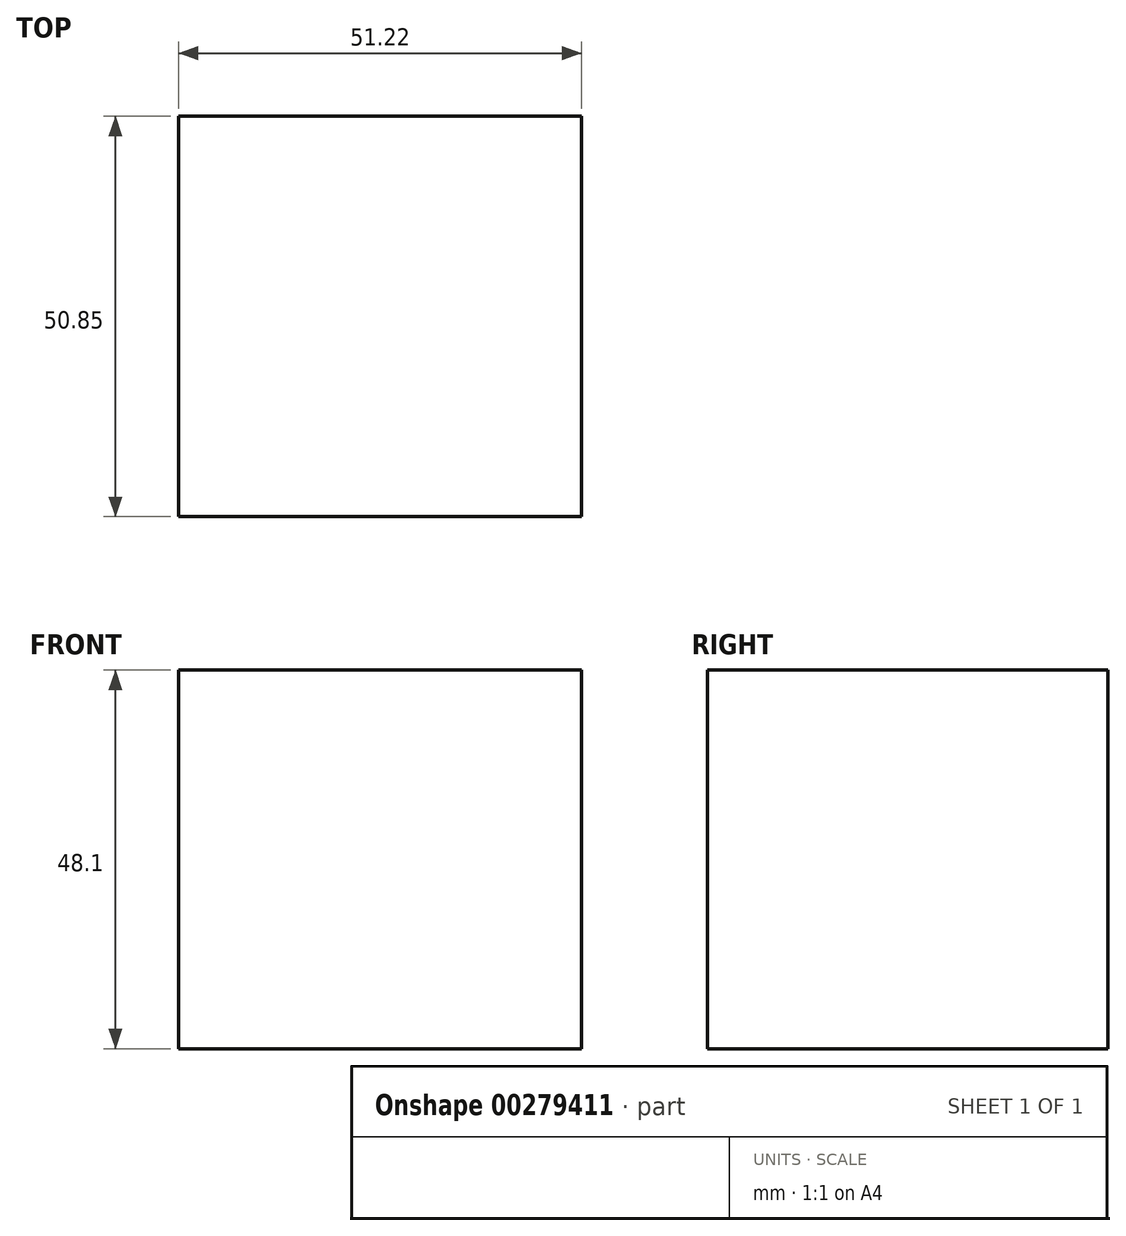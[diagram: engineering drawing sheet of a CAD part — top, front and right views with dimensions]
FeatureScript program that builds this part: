
annotation { "Feature Type Name" : "Feature", "Feature Type Description" : "" }
export const myFeature = defineFeature(function(context is Context, id is Id, definition is map)
    precondition{}
    {
        {
            var Q0;
            Q0=qCreatedBy(makeId("Top.planeOp"),FACE);
            var sketch = newSketch(context, id + "F0", { "sketchPlane" : qUnion([Q0])});
            skLineSegment(sketch, "E0.bottom", {"start": v(0, 0) * mm, "end": v(51.22, 0) * mm});
            skLineSegment(sketch, "E0.top", {"start": v(0, 50.85) * mm, "end": v(51.22, 50.85) * mm});
            skLineSegment(sketch, "E0.left", {"start": v(0, 0) * mm, "end": v(0, 50.85) * mm});
            skLineSegment(sketch, "E0.right", {"start": v(51.22, 0) * mm, "end": v(51.22, 50.85) * mm});
            skSolve(sketch);
        }
        {
            var Q0;
            Q0=makeQuery(id+"F0.imprint","IMPRINT",FACE,{"disambiguationData":[TD([[makeQuery(id+"F0.imprint","IMPRINT",EDGE,{"derivedFrom":sQuery(id+"F0.wireOp",EDGE,"E0.bottom")}),1.0]])]});
            extrude(context, id + "F1", {"entities" : qUnion([Q0]), "depth" : 48.1 * mm});
        }
        {
            var Q0;
            Q0=makeQuery(id+"F1.opExtrude","CAP_FACE",FACE,{"disambiguationData":[OSD([sQuery(id+"F0.wireOp",EDGE,"E0.bottom"),sQuery(id+"F0.wireOp",EDGE,"E0.top"),sQuery(id+"F0.wireOp",EDGE,"E0.left"),sQuery(id+"F0.wireOp",EDGE,"E0.right")])],"isStart":false});
            var sketch = newSketch(context, id + "F2", { "sketchPlane" : qUnion([Q0])});
            skLineSegment(sketch, "E1", {"start": v(0, 25.42) * mm, "end": v(51.22, 25.42) * mm});
            skSolve(sketch);
        }
        {
            var Q0;
            Q0=makeQuery(id+"F1.opExtrude","SWEPT_FACE",FACE,{"disambiguationData":[OSD([sQuery(id+"F0.wireOp",EDGE,"E0.left")])]});
            var sketch = newSketch(context, id + "F3", { "sketchPlane" : qUnion([Q0])});
            skLineSegment(sketch, "E2", {"start": v(-25.42, 48.1) * mm, "end": v(-25.42, 22.8) * mm});
            skLineSegment(sketch, "E3", {"start": v(-25.42, 22.8) * mm, "end": v(0, 22.8) * mm});
            skSolve(sketch);
        }
        {
            var Q0;
            {var subQ0=sQuery(id+"F3.wireOp",EDGE,"E2");Q0=makeQuery(id+"F3.imprint","IMPRINT",FACE,{"disambiguationData":[TD([[makeQuery(id+"F3.imprint","IMPRINT",EDGE,{"derivedFrom":subQ0}),1.0]])]});}
            extrude(context, id + "F4", {"entities" : qUnion([Q0]), "operationType" : NewBodyOperationType.ADD, "oppositeDirection" : true, "depth" : 48.1 * mm});
        }
        {
            var Q0;
            {var subQ0=sQuery(id+"F2.wireOp",EDGE,"E1");Q0=makeQuery(id+"F2.imprint","IMPRINT",FACE,{"disambiguationData":[TD([[makeQuery(id+"F2.imprint","IMPRINT",EDGE,{"derivedFrom":subQ0}),-1.0]])]});}
            extrude(context, id + "F5", {"entities" : qUnion([Q0]), "operationType" : NewBodyOperationType.ADD, "oppositeDirection" : true, "depth" : 25.4 * mm});
        }
    });
